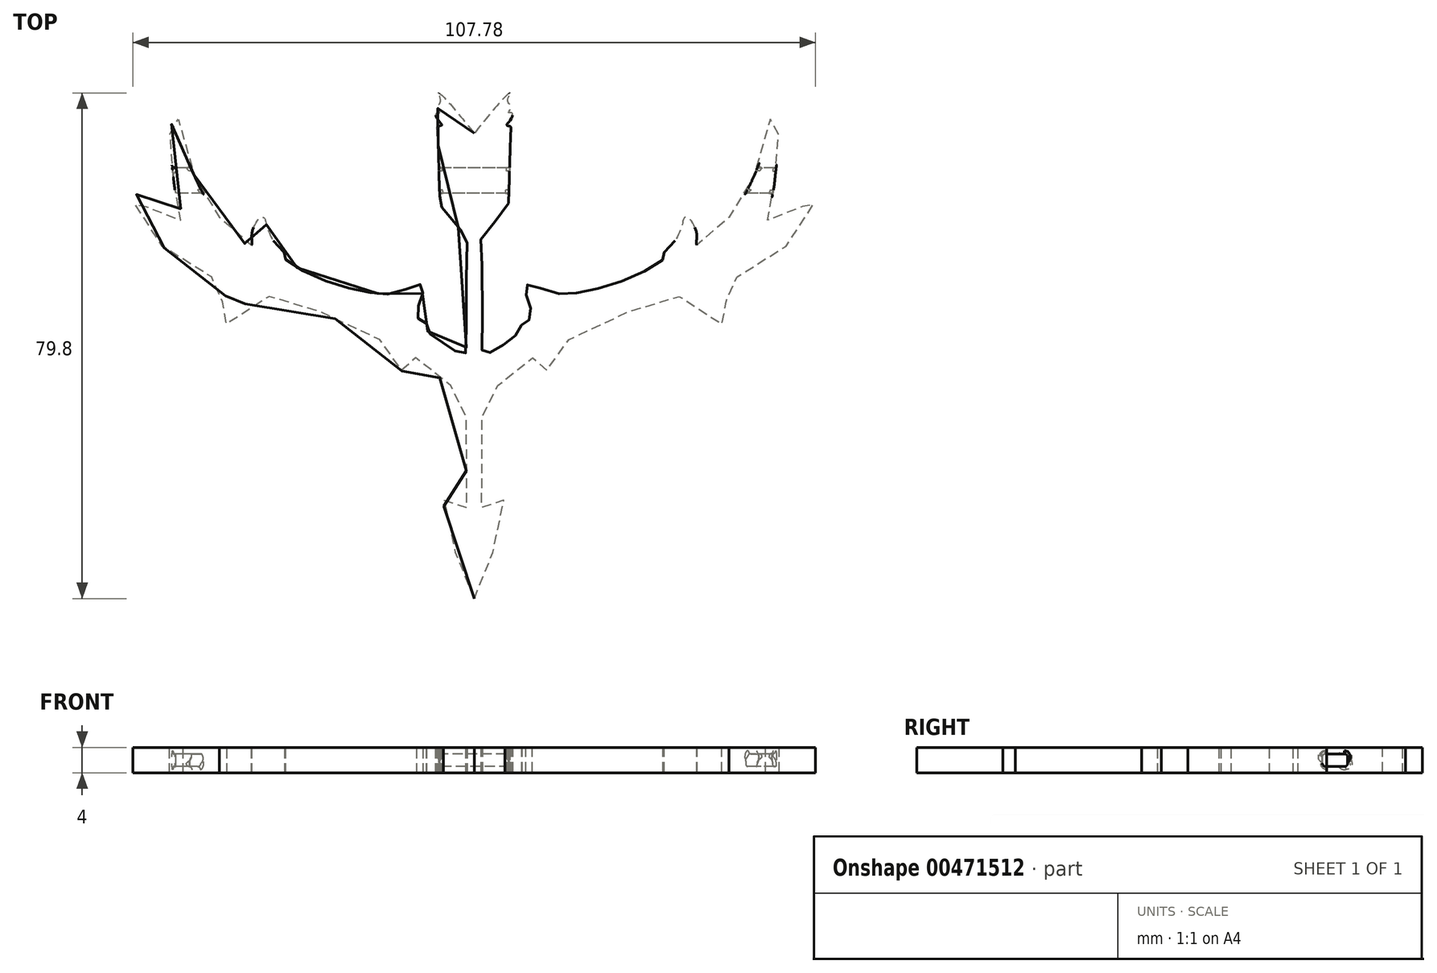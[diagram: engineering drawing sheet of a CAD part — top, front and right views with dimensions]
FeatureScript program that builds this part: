
annotation { "Feature Type Name" : "Feature", "Feature Type Description" : "" }
export const myFeature = defineFeature(function(context is Context, id is Id, definition is map)
    precondition{}
    {
        {
            var Q0;
            Q0=qCreatedBy(makeId("Top.planeOp"),FACE);
            var sketch = newSketch(context, id + "F0", { "sketchPlane" : qUnion([Q0])});
            skFitSpline(sketch, "E0", {"points": [v(0, -40) * mm, v(-1.78, -36.87) * mm, v(-3.82, -29.08) * mm, v(-4.75, -24.51) * mm, v(-3.22, -25.36) * mm, v(-1.53, -26.46) * mm, v(-1.2, -23.5) * mm, v(-1.28, -7.66) * mm, v(-1.44, -7.24) * mm, v(-3.82, -6.3) * mm, v(-8.3, -2.5) * mm, v(-9.23, -1.99) * mm, v(-9.83, -2.41) * mm, v(-10.25, -4.36) * mm, v(-11.18, -4.27) * mm, v(-12.28, -2.16) * mm, v(-13.64, 0) * mm, v(-21.09, 3.77) * mm, v(-27.1, 6.48) * mm, v(-32.77, 7.66) * mm, v(-37.85, 5.04) * mm, v(-39.8, 2.75) * mm, v(-40.23, 4.96) * mm, v(-39.55, 7.24) * mm, v(-39.04, 8.85) * mm, v(-40.73, 10.37) * mm, v(-45.9, 13) * mm, v(-51.4, 17.91) * mm, v(-53.43, 21.72) * mm, v(-53.86, 24.68) * mm, v(-52.76, 22.9) * mm, v(-48.44, 19.6) * mm, v(-46.83, 19.52) * mm, v(-45.98, 20.11) * mm, v(-46.83, 22.74) * mm, v(-47.68, 28.07) * mm, v(-48.1, 32.22) * mm, v(-47.25, 36.7) * mm, v(-46.91, 37.13) * mm, v(-46.6, 34.12) * mm, v(-44.12, 26.61) * mm, v(-42.46, 23.34) * mm, v(-38.96, 18.68) * mm, v(-35.66, 15.72) * mm, v(-35.11, 15.85) * mm, v(-35.11, 17.58) * mm, v(-33.71, 20.12) * mm, v(-33.12, 20.04) * mm, v(-32.9, 19.36) * mm, v(-31.98, 16.95) * mm, v(-30.33, 14.91) * mm, v(-29.73, 14.32) * mm, v(-29.9, 13.81) * mm, v(-27.79, 12.12) * mm, v(-22.92, 9.92) * mm, v(-18, 8.56) * mm, v(-14.66, 8.1) * mm, v(-12.16, 8.31) * mm, v(-9.07, 9.54) * mm, v(-8.35, 9.5) * mm, v(-8.06, 8.82) * mm, v(-8.4, 7.38) * mm, v(-8.95, 5.77) * mm, v(-8.99, 4.42) * mm, v(-8.1, 3.65) * mm, v(-7.5, 3.36) * mm, v(-7.47, 2.38) * mm, v(-5.98, 1.16) * mm, v(-4.49, 0) * mm, v(-2.68, -1.09) * mm, v(-1.52, -1.39) * mm, v(-1.24, 0.4) * mm, v(-1.11, 16.18) * mm, v(-1.2, 16.99) * mm, v(-5.22, 21.9) * mm, v(-5.43, 22.83) * mm, v(-5.52, 25.45) * mm, v(-5.77, 33.75) * mm, v(-5.64, 34.56) * mm, v(-5.13, 34.73) * mm, v(-5.9, 35.83) * mm, v(-5.9, 36.67) * mm, v(-5.43, 36.67) * mm, v(-5.77, 37.6) * mm, v(-5.3, 38.5) * mm, v(-5.6, 39.76) * mm, v(-4.67, 39) * mm, v(0, 33.41) * mm], "startDerivative": vector(-141.4, 200.73) * mm, "endDerivative": vector(270.57, -337.6) * mm});
            skFitSpline(sketch, "E1.MirrorCS", {"points": [v(0, -40) * mm, v(1.78, -36.87) * mm, v(3.82, -29.08) * mm, v(4.75, -24.51) * mm, v(3.22, -25.36) * mm, v(1.53, -26.46) * mm, v(1.2, -23.5) * mm, v(1.28, -7.66) * mm, v(1.44, -7.24) * mm, v(3.82, -6.3) * mm, v(8.3, -2.5) * mm, v(9.23, -1.99) * mm, v(9.83, -2.41) * mm, v(10.25, -4.36) * mm, v(11.18, -4.27) * mm, v(12.28, -2.16) * mm, v(13.64, 0) * mm, v(21.09, 3.77) * mm, v(27.1, 6.48) * mm, v(32.77, 7.66) * mm, v(37.85, 5.04) * mm, v(39.8, 2.75) * mm, v(40.23, 4.96) * mm, v(39.55, 7.24) * mm, v(39.04, 8.85) * mm, v(40.73, 10.37) * mm, v(45.9, 13) * mm, v(51.4, 17.91) * mm, v(53.43, 21.72) * mm, v(53.86, 24.68) * mm, v(52.76, 22.9) * mm, v(48.44, 19.6) * mm, v(46.83, 19.52) * mm, v(45.98, 20.11) * mm, v(46.83, 22.74) * mm, v(47.68, 28.07) * mm, v(48.1, 32.22) * mm, v(47.25, 36.7) * mm, v(46.91, 37.13) * mm, v(46.6, 34.12) * mm, v(44.12, 26.61) * mm, v(42.46, 23.34) * mm, v(38.96, 18.68) * mm, v(35.66, 15.72) * mm, v(35.11, 15.85) * mm, v(35.11, 17.58) * mm, v(33.71, 20.12) * mm, v(33.12, 20.04) * mm, v(32.9, 19.36) * mm, v(31.98, 16.95) * mm, v(30.33, 14.91) * mm, v(29.73, 14.32) * mm, v(29.9, 13.81) * mm, v(27.79, 12.12) * mm, v(22.92, 9.92) * mm, v(18, 8.56) * mm, v(14.66, 8.1) * mm, v(12.16, 8.31) * mm, v(9.07, 9.54) * mm, v(8.35, 9.5) * mm, v(8.06, 8.82) * mm, v(8.4, 7.38) * mm, v(8.95, 5.77) * mm, v(8.99, 4.42) * mm, v(8.1, 3.65) * mm, v(7.5, 3.36) * mm, v(7.47, 2.38) * mm, v(5.98, 1.16) * mm, v(4.49, 0) * mm, v(2.68, -1.09) * mm, v(1.52, -1.39) * mm, v(1.24, 0.4) * mm, v(1.11, 16.18) * mm, v(1.2, 16.99) * mm, v(5.22, 21.9) * mm, v(5.43, 22.83) * mm, v(5.52, 25.45) * mm, v(5.77, 33.75) * mm, v(5.64, 34.56) * mm, v(5.13, 34.73) * mm, v(5.9, 35.83) * mm, v(5.9, 36.67) * mm, v(5.43, 36.67) * mm, v(5.77, 37.6) * mm, v(5.3, 38.5) * mm, v(5.6, 39.76) * mm, v(4.67, 39) * mm, v(0, 33.41) * mm], "startDerivative": vector(141.4, 200.73) * mm, "endDerivative": vector(-270.57, -337.6) * mm});
            skSolve(sketch);
        }
        {
            var Q0;
            Q0 = qSketchRegion(id + "F0", true);
            extrude(context, id + "F1", {"entities" : qUnion([Q0]), "depth" : 4 * mm});
        }
        {
            var Q0;
            Q0=makeQuery(id+"F1.opExtrude","CAP_FACE",FACE,{"disambiguationData":[OSD([sQuery(id+"F0.wireOp",EDGE,"E0"),sQuery(id+"F0.wireOp",EDGE,"E1.MirrorCS")])],"isStart":false});
            cPlane(context, id + "F2", {"entities" : qUnion([Q0]), "cplaneType" : CPlaneType.OFFSET, "offset" : 0 * mm, "width" : 150 * mm, "height" : 150 * mm});
        }
        {
            var Q0;
            Q0=qCreatedBy(makeId("Right.planeOp"),FACE);
            var sketch = newSketch(context, id + "F3", { "sketchPlane" : qUnion([Q0])});
            skLineSegment(sketch, "E2.bottom", {"start": v(28, 1) * mm, "end": v(24, 1) * mm});
            skLineSegment(sketch, "E2.top", {"start": v(28, 3) * mm, "end": v(24, 3) * mm});
            skLineSegment(sketch, "E2.left", {"start": v(28, 1) * mm, "end": v(28, 3) * mm});
            skLineSegment(sketch, "E2.right", {"start": v(24, 1) * mm, "end": v(24, 3) * mm});
            skSolve(sketch);
        }
        {
            var Q0;
            Q0 = qSketchRegion(id + "F3", true);
            extrude(context, id + "F4", {"entities" : qUnion([Q0]), "operationType" : NewBodyOperationType.REMOVE, "endBound" : BoundingType.SYMMETRIC, "depth" : 100 * mm});
        }
        {
            var Q0;
            {var subQ0=sQuery(id+"F3.wireOp",EDGE,"E2.bottom");var subQ1=sQuery(id+"F3.wireOp",EDGE,"E2.right");Q0=makeQuery(id+"F4.boolean.opBoolean","COPY",EDGE,{"disambiguationData":[TD([makeQuery(id+"F1.opExtrude","SWEPT_FACE",FACE,{"disambiguationData":[OSD([sQuery(id+"F0.wireOp",EDGE,"E1.MirrorCS")])]}),makeQuery(id+"F4.opExtrude","SWEPT_FACE",FACE,{"disambiguationData":[OSD([subQ0])]}),makeQuery(id+"F4.opExtrude","SWEPT_FACE",FACE,{"disambiguationData":[OSD([subQ1])]})])],"derivedFrom":makeQuery(id+"F4.opExtrude","SWEPT_EDGE",EDGE,{"disambiguationData":[OSD([subQ0,subQ1])]})});}
            var Q1;
            {var subQ0=sQuery(id+"F3.wireOp",EDGE,"E2.top");var subQ1=sQuery(id+"F3.wireOp",EDGE,"E2.right");Q1=makeQuery(id+"F4.boolean.opBoolean","COPY",EDGE,{"disambiguationData":[TD([makeQuery(id+"F1.opExtrude","SWEPT_FACE",FACE,{"disambiguationData":[OSD([sQuery(id+"F0.wireOp",EDGE,"E1.MirrorCS")])]}),makeQuery(id+"F4.opExtrude","SWEPT_FACE",FACE,{"disambiguationData":[OSD([subQ0])]}),makeQuery(id+"F4.opExtrude","SWEPT_FACE",FACE,{"disambiguationData":[OSD([subQ1])]})])],"derivedFrom":makeQuery(id+"F4.opExtrude","SWEPT_EDGE",EDGE,{"disambiguationData":[OSD([subQ0,subQ1])]})});}
            var Q2;
            {var subQ0=sQuery(id+"F3.wireOp",EDGE,"E2.left");var subQ1=sQuery(id+"F3.wireOp",EDGE,"E2.top");Q2=makeQuery(id+"F4.boolean.opBoolean","COPY",EDGE,{"disambiguationData":[TD([makeQuery(id+"F1.opExtrude","SWEPT_FACE",FACE,{"disambiguationData":[OSD([sQuery(id+"F0.wireOp",EDGE,"E1.MirrorCS")])]}),makeQuery(id+"F4.opExtrude","SWEPT_FACE",FACE,{"disambiguationData":[OSD([subQ1])]}),makeQuery(id+"F4.opExtrude","SWEPT_FACE",FACE,{"disambiguationData":[OSD([subQ0])]})])],"derivedFrom":makeQuery(id+"F4.opExtrude","SWEPT_EDGE",EDGE,{"disambiguationData":[OSD([subQ1,subQ0])]})});}
            var Q3;
            {var subQ0=sQuery(id+"F3.wireOp",EDGE,"E2.left");var subQ1=sQuery(id+"F3.wireOp",EDGE,"E2.bottom");Q3=makeQuery(id+"F4.boolean.opBoolean","COPY",EDGE,{"disambiguationData":[TD([makeQuery(id+"F1.opExtrude","SWEPT_FACE",FACE,{"disambiguationData":[OSD([sQuery(id+"F0.wireOp",EDGE,"E1.MirrorCS")])]}),makeQuery(id+"F4.opExtrude","SWEPT_FACE",FACE,{"disambiguationData":[OSD([subQ1])]}),makeQuery(id+"F4.opExtrude","SWEPT_FACE",FACE,{"disambiguationData":[OSD([subQ0])]})])],"derivedFrom":makeQuery(id+"F4.opExtrude","SWEPT_EDGE",EDGE,{"disambiguationData":[OSD([subQ1,subQ0])]})});}
            var Q4;
            {var subQ0=sQuery(id+"F3.wireOp",EDGE,"E2.bottom");var subQ1=sQuery(id+"F3.wireOp",EDGE,"E2.right");Q4=makeQuery(id+"F4.boolean.opBoolean","COPY",EDGE,{"disambiguationData":[TD([makeQuery(id+"F1.opExtrude","SWEPT_FACE",FACE,{"disambiguationData":[OSD([sQuery(id+"F0.wireOp",EDGE,"E0")])]}),makeQuery(id+"F1.opExtrude","SWEPT_FACE",FACE,{"disambiguationData":[OSD([sQuery(id+"F0.wireOp",EDGE,"E1.MirrorCS")])]}),makeQuery(id+"F4.opExtrude","SWEPT_FACE",FACE,{"disambiguationData":[OSD([subQ0])]}),makeQuery(id+"F4.opExtrude","SWEPT_FACE",FACE,{"disambiguationData":[OSD([subQ1])]})])],"derivedFrom":makeQuery(id+"F4.opExtrude","SWEPT_EDGE",EDGE,{"disambiguationData":[OSD([subQ0,subQ1])]})});}
            var Q5;
            {var subQ0=sQuery(id+"F3.wireOp",EDGE,"E2.top");var subQ1=sQuery(id+"F3.wireOp",EDGE,"E2.right");Q5=makeQuery(id+"F4.boolean.opBoolean","COPY",EDGE,{"disambiguationData":[TD([makeQuery(id+"F1.opExtrude","SWEPT_FACE",FACE,{"disambiguationData":[OSD([sQuery(id+"F0.wireOp",EDGE,"E0")])]}),makeQuery(id+"F1.opExtrude","SWEPT_FACE",FACE,{"disambiguationData":[OSD([sQuery(id+"F0.wireOp",EDGE,"E1.MirrorCS")])]}),makeQuery(id+"F4.opExtrude","SWEPT_FACE",FACE,{"disambiguationData":[OSD([subQ0])]}),makeQuery(id+"F4.opExtrude","SWEPT_FACE",FACE,{"disambiguationData":[OSD([subQ1])]})])],"derivedFrom":makeQuery(id+"F4.opExtrude","SWEPT_EDGE",EDGE,{"disambiguationData":[OSD([subQ0,subQ1])]})});}
            var Q6;
            {var subQ0=sQuery(id+"F3.wireOp",EDGE,"E2.left");var subQ1=sQuery(id+"F3.wireOp",EDGE,"E2.bottom");Q6=makeQuery(id+"F4.boolean.opBoolean","COPY",EDGE,{"disambiguationData":[TD([makeQuery(id+"F1.opExtrude","SWEPT_FACE",FACE,{"disambiguationData":[OSD([sQuery(id+"F0.wireOp",EDGE,"E0")])]}),makeQuery(id+"F1.opExtrude","SWEPT_FACE",FACE,{"disambiguationData":[OSD([sQuery(id+"F0.wireOp",EDGE,"E1.MirrorCS")])]}),makeQuery(id+"F4.opExtrude","SWEPT_FACE",FACE,{"disambiguationData":[OSD([subQ1])]}),makeQuery(id+"F4.opExtrude","SWEPT_FACE",FACE,{"disambiguationData":[OSD([subQ0])]})])],"derivedFrom":makeQuery(id+"F4.opExtrude","SWEPT_EDGE",EDGE,{"disambiguationData":[OSD([subQ1,subQ0])]})});}
            var Q7;
            {var subQ0=sQuery(id+"F3.wireOp",EDGE,"E2.left");var subQ1=sQuery(id+"F3.wireOp",EDGE,"E2.top");Q7=makeQuery(id+"F4.boolean.opBoolean","COPY",EDGE,{"disambiguationData":[TD([makeQuery(id+"F1.opExtrude","SWEPT_FACE",FACE,{"disambiguationData":[OSD([sQuery(id+"F0.wireOp",EDGE,"E0")])]}),makeQuery(id+"F1.opExtrude","SWEPT_FACE",FACE,{"disambiguationData":[OSD([sQuery(id+"F0.wireOp",EDGE,"E1.MirrorCS")])]}),makeQuery(id+"F4.opExtrude","SWEPT_FACE",FACE,{"disambiguationData":[OSD([subQ1])]}),makeQuery(id+"F4.opExtrude","SWEPT_FACE",FACE,{"disambiguationData":[OSD([subQ0])]})])],"derivedFrom":makeQuery(id+"F4.opExtrude","SWEPT_EDGE",EDGE,{"disambiguationData":[OSD([subQ1,subQ0])]})});}
            var Q8;
            {var subQ0=sQuery(id+"F3.wireOp",EDGE,"E2.bottom");var subQ1=sQuery(id+"F3.wireOp",EDGE,"E2.left");Q8=makeQuery(id+"F4.boolean.opBoolean","COPY",EDGE,{"disambiguationData":[TD([makeQuery(id+"F1.opExtrude","SWEPT_FACE",FACE,{"disambiguationData":[OSD([sQuery(id+"F0.wireOp",EDGE,"E0")])]}),makeQuery(id+"F4.opExtrude","SWEPT_FACE",FACE,{"disambiguationData":[OSD([subQ0])]}),makeQuery(id+"F4.opExtrude","SWEPT_FACE",FACE,{"disambiguationData":[OSD([subQ1])]})])],"derivedFrom":makeQuery(id+"F4.opExtrude","SWEPT_EDGE",EDGE,{"disambiguationData":[OSD([subQ0,subQ1])]})});}
            var Q9;
            {var subQ0=sQuery(id+"F3.wireOp",EDGE,"E2.top");var subQ1=sQuery(id+"F3.wireOp",EDGE,"E2.left");Q9=makeQuery(id+"F4.boolean.opBoolean","COPY",EDGE,{"disambiguationData":[TD([makeQuery(id+"F1.opExtrude","SWEPT_FACE",FACE,{"disambiguationData":[OSD([sQuery(id+"F0.wireOp",EDGE,"E0")])]}),makeQuery(id+"F4.opExtrude","SWEPT_FACE",FACE,{"disambiguationData":[OSD([subQ0])]}),makeQuery(id+"F4.opExtrude","SWEPT_FACE",FACE,{"disambiguationData":[OSD([subQ1])]})])],"derivedFrom":makeQuery(id+"F4.opExtrude","SWEPT_EDGE",EDGE,{"disambiguationData":[OSD([subQ0,subQ1])]})});}
            var Q10;
            {var subQ0=sQuery(id+"F3.wireOp",EDGE,"E2.top");var subQ1=sQuery(id+"F3.wireOp",EDGE,"E2.right");Q10=makeQuery(id+"F4.boolean.opBoolean","COPY",EDGE,{"disambiguationData":[TD([makeQuery(id+"F1.opExtrude","SWEPT_FACE",FACE,{"disambiguationData":[OSD([sQuery(id+"F0.wireOp",EDGE,"E0")])]}),makeQuery(id+"F4.opExtrude","SWEPT_FACE",FACE,{"disambiguationData":[OSD([subQ0])]}),makeQuery(id+"F4.opExtrude","SWEPT_FACE",FACE,{"disambiguationData":[OSD([subQ1])]})])],"derivedFrom":makeQuery(id+"F4.opExtrude","SWEPT_EDGE",EDGE,{"disambiguationData":[OSD([subQ0,subQ1])]})});}
            var Q11;
            {var subQ0=sQuery(id+"F3.wireOp",EDGE,"E2.bottom");var subQ1=sQuery(id+"F3.wireOp",EDGE,"E2.right");Q11=makeQuery(id+"F4.boolean.opBoolean","COPY",EDGE,{"disambiguationData":[TD([makeQuery(id+"F1.opExtrude","SWEPT_FACE",FACE,{"disambiguationData":[OSD([sQuery(id+"F0.wireOp",EDGE,"E0")])]}),makeQuery(id+"F4.opExtrude","SWEPT_FACE",FACE,{"disambiguationData":[OSD([subQ0])]}),makeQuery(id+"F4.opExtrude","SWEPT_FACE",FACE,{"disambiguationData":[OSD([subQ1])]})])],"derivedFrom":makeQuery(id+"F4.opExtrude","SWEPT_EDGE",EDGE,{"disambiguationData":[OSD([subQ0,subQ1])]})});}
            var Q12;
            Q12=makeQuery(id+"F4.boolean.opBoolean","INTERSECT",EDGE,{"disambiguationData":[OD(2.0)],"derivedFrom":[makeQuery(id+"F1.opExtrude","SWEPT_FACE",FACE,{"disambiguationData":[OSD([sQuery(id+"F0.wireOp",EDGE,"E0")])]}),makeQuery(id+"F4.opExtrude","SWEPT_FACE",FACE,{"disambiguationData":[OSD([sQuery(id+"F3.wireOp",EDGE,"E2.bottom")])]})]});
            var Q13;
            Q13=makeQuery(id+"F4.boolean.opBoolean","INTERSECT",EDGE,{"disambiguationData":[OD(1.0)],"derivedFrom":[makeQuery(id+"F1.opExtrude","SWEPT_FACE",FACE,{"disambiguationData":[OSD([sQuery(id+"F0.wireOp",EDGE,"E0")])]}),makeQuery(id+"F4.opExtrude","SWEPT_FACE",FACE,{"disambiguationData":[OSD([sQuery(id+"F3.wireOp",EDGE,"E2.left")])]})]});
            var Q14;
            Q14=makeQuery(id+"F4.boolean.opBoolean","INTERSECT",EDGE,{"disambiguationData":[OD(0.0)],"derivedFrom":[makeQuery(id+"F1.opExtrude","SWEPT_FACE",FACE,{"disambiguationData":[OSD([sQuery(id+"F0.wireOp",EDGE,"E0")])]}),makeQuery(id+"F4.opExtrude","SWEPT_FACE",FACE,{"disambiguationData":[OSD([sQuery(id+"F3.wireOp",EDGE,"E2.top")])]})]});
            var Q15;
            Q15=makeQuery(id+"F4.boolean.opBoolean","INTERSECT",EDGE,{"disambiguationData":[OD(0.0)],"derivedFrom":[makeQuery(id+"F1.opExtrude","SWEPT_FACE",FACE,{"disambiguationData":[OSD([sQuery(id+"F0.wireOp",EDGE,"E1.MirrorCS")])]}),makeQuery(id+"F4.opExtrude","SWEPT_FACE",FACE,{"disambiguationData":[OSD([sQuery(id+"F3.wireOp",EDGE,"E2.top")])]})]});
            var Q16;
            Q16=makeQuery(id+"F4.boolean.opBoolean","INTERSECT",EDGE,{"disambiguationData":[OD(2.0)],"derivedFrom":[makeQuery(id+"F1.opExtrude","SWEPT_FACE",FACE,{"disambiguationData":[OSD([sQuery(id+"F0.wireOp",EDGE,"E1.MirrorCS")])]}),makeQuery(id+"F4.opExtrude","SWEPT_FACE",FACE,{"disambiguationData":[OSD([sQuery(id+"F3.wireOp",EDGE,"E2.top")])]})]});
            var Q17;
            Q17=makeQuery(id+"F4.boolean.opBoolean","INTERSECT",EDGE,{"disambiguationData":[OD(1.0)],"derivedFrom":[makeQuery(id+"F1.opExtrude","SWEPT_FACE",FACE,{"disambiguationData":[OSD([sQuery(id+"F0.wireOp",EDGE,"E1.MirrorCS")])]}),makeQuery(id+"F4.opExtrude","SWEPT_FACE",FACE,{"disambiguationData":[OSD([sQuery(id+"F3.wireOp",EDGE,"E2.top")])]})]});
            fillet(context, id + "F5", {"entities" : qUnion([Q0, Q1, Q2, Q3, Q4, Q5, Q6, Q7, Q8, Q9, Q10, Q11, Q12, Q13, Q14, Q15, Q16, Q17]), "radius" : 0.5 * mm, "tangentPropagation" : true, "allowEdgeOverflow" : false});
        }
    });
